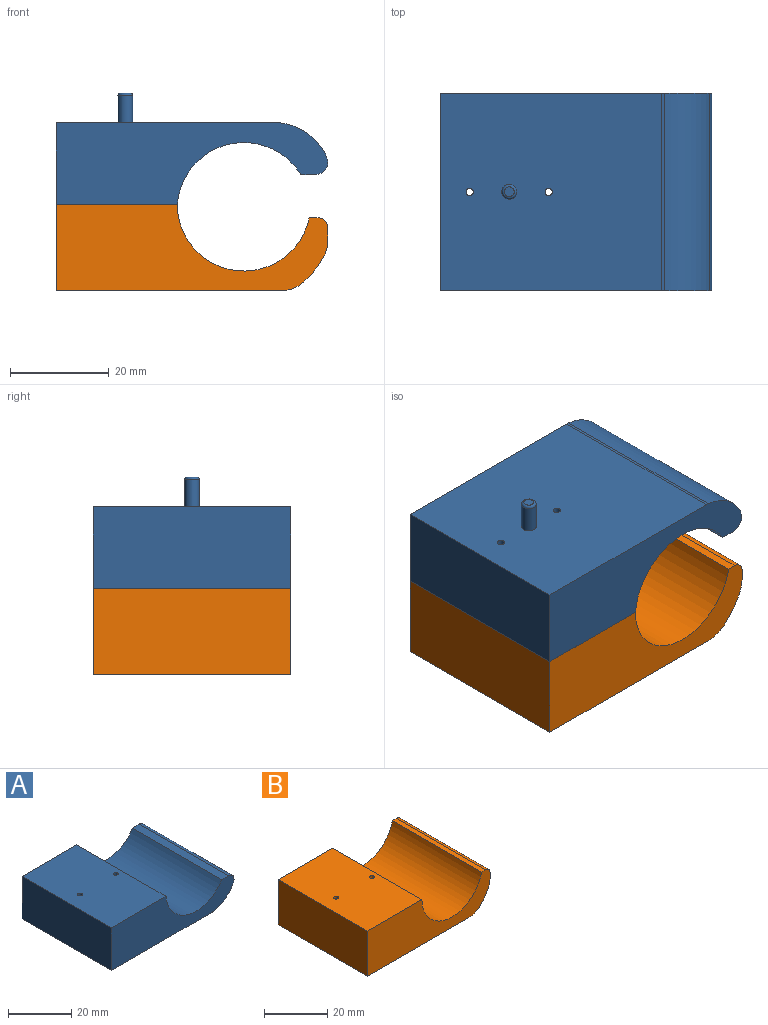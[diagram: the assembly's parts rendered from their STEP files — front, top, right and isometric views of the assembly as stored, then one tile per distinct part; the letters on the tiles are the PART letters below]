
ASSEMBLY  parts=2 mates=1
PART A: 16 faces, bbox 55x40x22.5 mm
  f0: plane 55x16.5mm, normal (0,1,0), area 599.1mm2, adj f2,f5,f6,f10,f11,f12,f13,f14
  f1: plane 55x16.5mm, normal (0,-1,0), area 599.1mm2, adj f2,f5,f6,f10,f11,f12,f13,f14
  f2: plane 40x16.5mm, normal (-1,0,0), area 660mm2, adj f0,f1,f5,f6
  f3: cylinder r=0.75mm len=16.5mm, axis (0,0,-1), area 77.8mm2, adj f5,f6
  f4: cylinder r=0.75mm len=16.5mm, axis (0,0,-1), area 77.8mm2, adj f5,f6
  f5: plane 40x24.54mm, normal (0,0,1), area 977.9mm2, adj f0,f1,f2,f3,f4,f11
  f6: plane 44.81x40mm, normal (0,0,-1), area 1781.8mm2, adj f0,f1,f2,f3,f4,f7,f15
  f7: cylinder r=1.5mm len=5.5mm, axis (0,0,1), area 51.8mm2, adj f6,f9
  f8: plane 2x2mm, normal (0,0,-1), area 3.1mm2, adj f9
  f9: torus R=1mm, axis (0,0,1), area 6.5mm2, adj f7,f8
  f10: plane 40x2.98mm, normal (0,0,1), area 119.1mm2, adj f0,f1,f11,f13
  f11: cylinder r=13.5mm len=40mm, axis (0,-1,0), area 1360.5mm2, adj f0,f1,f5,f10
  f12: cylinder r=11.75mm len=40mm, axis (0,-1,0), area 459.6mm2, adj f0,f1,f14,f15
  f13: cylinder r=2.5mm len=40mm, axis (0,-1,0), area 157.1mm2, adj f0,f1,f10,f14
  f14: cylinder r=5mm len=40mm, axis (0,-1,0), area 71.1mm2, adj f0,f1,f12,f13
  f15: cylinder r=5mm len=40mm, axis (0,-1,0), area 22.5mm2, adj f0,f1,f6,f12
PART B: 14 faces, bbox 55x40x17.5 mm
  f0: plane 40x2.53mm, normal (1,0,0), area 101.3mm2, adj f1,f2,f11,f12
  f1: plane 55x17.5mm, normal (0,1,0), area 639.9mm2, adj f0,f3,f6,f7,f8,f9,f10,f11
  f2: plane 55x17.5mm, normal (0,-1,0), area 639.9mm2, adj f0,f3,f6,f7,f8,f9,f10,f11
  f3: plane 40x17.5mm, normal (-1,0,0), area 700mm2, adj f1,f2,f6,f7
  f4: cylinder r=0.75mm len=17.5mm, axis (0,0,-1), area 82.5mm2, adj f6,f7
  f5: cylinder r=0.75mm len=17.5mm, axis (0,0,-1), area 82.5mm2, adj f6,f7
  f6: plane 40x24.5mm, normal (0,0,1), area 976.5mm2, adj f1,f2,f3,f4,f5,f9
  f7: plane 45.45x40mm, normal (0,0,-1), area 1814.3mm2, adj f1,f2,f3,f4,f5,f13
  f8: plane 40x1.78mm, normal (0,0,1), area 71mm2, adj f1,f2,f9,f11
  f9: cylinder r=13.5mm len=40mm, axis (0,-1,0), area 1587mm2, adj f1,f2,f6,f8
  f10: cylinder r=18.88mm len=40mm, axis (0,-1,0), area 264.1mm2, adj f1,f2,f12,f13
  f11: cylinder r=2mm len=40mm, axis (0,-1,0), area 125.7mm2, adj f0,f1,f2,f8
  f12: cylinder r=7mm len=40mm, axis (0,-1,0), area 137.4mm2, adj f0,f1,f2,f10
  f13: cylinder r=7mm len=40mm, axis (0,-1,0), area 204.5mm2, adj f1,f2,f7,f10
PLACE A rot(axis=(1,0,0),180deg) t=(-0.02,0,34)mm
PLACE B at identity
MATE revolute A.f5 <-> B.f6  axis (0,0,-1) through (-15.26,0,17.5)mm
